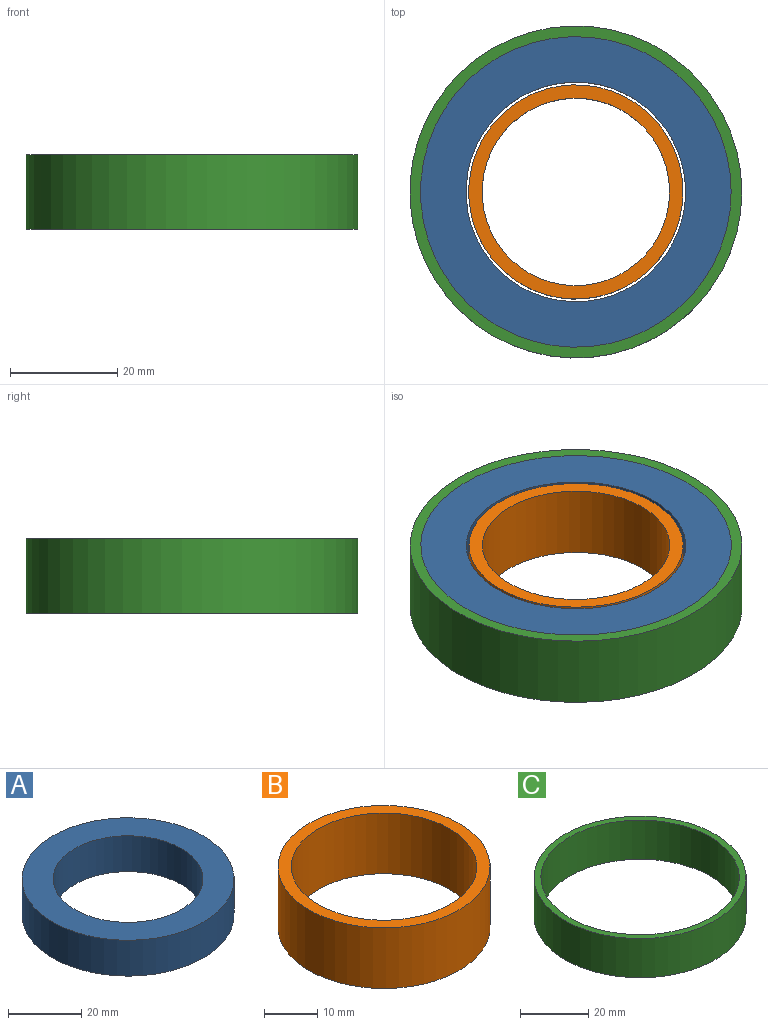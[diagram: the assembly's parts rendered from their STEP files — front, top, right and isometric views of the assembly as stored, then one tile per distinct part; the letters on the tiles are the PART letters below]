
ASSEMBLY  parts=3 mates=2
PART A: 4 faces, bbox 58x58x12 mm
  f0: cylinder r=20.5mm len=41mm, axis (0,0,-1), area 1545.7mm2, adj f2,f3
  f1: cylinder r=29mm len=58mm, axis (0,0,-1), area 2186.5mm2, adj f2,f3
  f2: plane 58x58mm, normal (0,0,1), area 1321.8mm2, adj f0,f1
  f3: plane 58x58mm, normal (0,0,-1), area 1321.8mm2, adj f0,f1
PART B: 4 faces, bbox 40x40x14 mm
  f0: cylinder r=17.5mm len=35mm, axis (0,0,-1), area 1539.4mm2, adj f2,f3
  f1: cylinder r=20mm len=40mm, axis (0,0,-1), area 1759.3mm2, adj f2,f3
  f2: plane 40x40mm, normal (0,0,1), area 294.5mm2, adj f0,f1
  f3: plane 40x40mm, normal (0,0,-1), area 294.5mm2, adj f0,f1
PART C: 4 faces, bbox 62x62x14 mm
  f0: cylinder r=29mm len=58mm, axis (0,0,-1), area 2551mm2, adj f2,f3
  f1: cylinder r=31mm len=62mm, axis (0,0,-1), area 2726.9mm2, adj f2,f3
  f2: plane 62x62mm, normal (0,0,1), area 377mm2, adj f0,f1
  f3: plane 62x62mm, normal (0,0,-1), area 377mm2, adj f0,f1
PLACE A t=(37.16,-20.34,-0.91)mm
PLACE B rot(axis=(1,0,0),180deg) t=(37.16,-20.34,12.09)mm
PLACE C t=(37.16,-20.34,-1.91)mm
MATE fastened C.f0 <-> B.f0  axis (0,0,1) through (37.16,-20.34,12.09)mm
MATE fastened B.f0 <-> A.f0  axis (0,0,1) through (37.16,-20.34,12.09)mm
